# Revit family: Column Bases-End
name_source: partatom
category: Detail Items
revit_build: Autodesk Revit Architecture 2012 (Build: 20110210_1515)
units: mm (PartAtom-declared; Revit-internal decimal feet)

## types (13) — shared parameters
Depth = 8"
Finish = Gray Paint

## per-type parameters (varying)
| type | Hole Diameter | Keynote | Plate Thickness | Post Size | Strap Width | Width End | Width Side | r |
| CB44 | 11/16" | 06 05 23.E1 | 3/16" | 4x4 | 2" | 3 9/16" | 3 1/2" | 11/32" |
| CB46 | 11/16" | 06 05 23.E2 | 3/16" | 4x6 | 2" | 3 9/16" | 5 1/2" | 11/32" |
| CB48 | 11/16" | 06 05 23.E3 | 3/16" | 4x8 | 2" | 3 9/16" | 7 1/2" | 11/32" |
| CB66 | 11/16" | 06 05 23.E4 | 3/16" | 6x6 | 3" | 5 1/2" | 5 1/2" | 11/32" |
| CB68 | 11/16" | 06 05 23.E5 | 3/16" | 6x8 | 3" | 5 1/2" | 7 1/2" | 11/32" |
| CB610 | 11/16" | 06 05 23.E6 | 3/16" | 6x10 | 3" | 5 1/2" | 9 1/2" | 11/32" |
| CB612 | 11/16" | 06 05 23.E7 | 3/16" | 6x12 | 3" | 5 1/2" | 11 1/2" | 11/32" |
| CB88 | 13/16" | 06 05 23.E8 | 3/16" | 8x8 | 3" | 7 1/2" | 7 1/2" | 13/32" |
| CB810 | 13/16" | 06 05 23.E9 | 3/16" | 8x10 | 3" | 7 1/2" | 9 1/2" | 13/32" |
| CB812 | 13/16" | 06 05 23.E10 | 3/16" | 8x12 | 3" | 7 1/2" | 11 1/2" | 13/32" |
| CB1010 | 13/16" | 06 05 23.E11 | 1/4" | 10x10 | 3" | 9 1/2" | 9 1/2" | 13/32" |
| CB1012 | 13/16" | 06 05 23.E12 | 1/4" | 10x12 | 3" | 9 1/2" | 11 1/2" | 13/32" |
| CB1212 | 13/16" | 06 05 23.E13 | 1/4" | 12x12 | 3" | 11 1/2" | 11 1/2" | 13/32" |

## geometry (parser evidence)
native form markers: Sweep x1
no freeform markers — native parametric forms only
